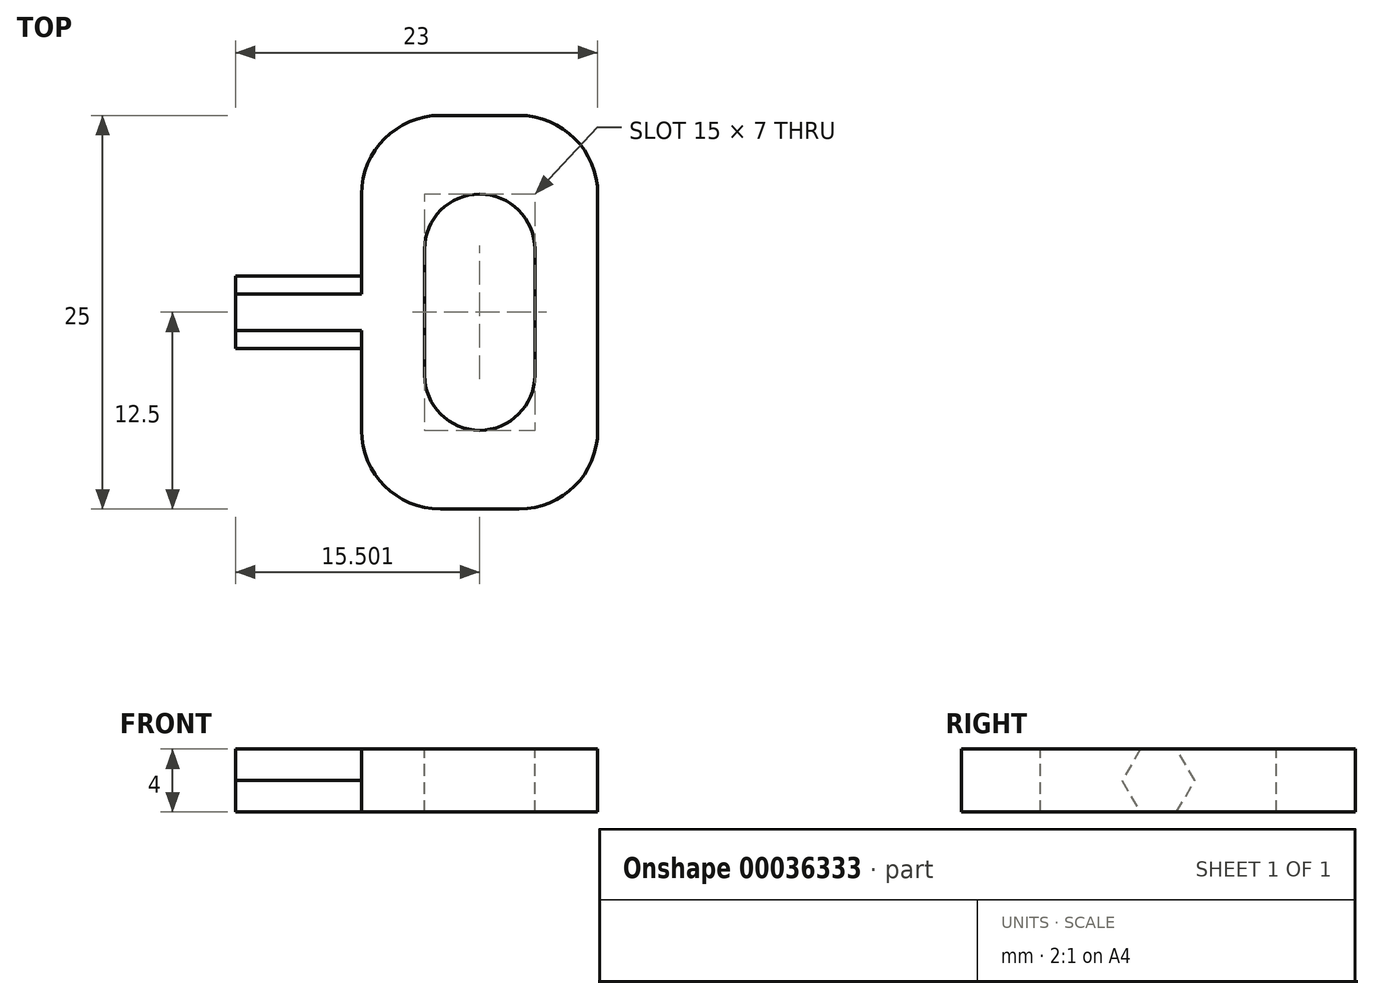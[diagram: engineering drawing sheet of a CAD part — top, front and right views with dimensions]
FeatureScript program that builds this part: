
annotation { "Feature Type Name" : "Feature", "Feature Type Description" : "" }
export const myFeature = defineFeature(function(context is Context, id is Id, definition is map)
    precondition{}
    {
        {
            var Q0;
            Q0=qCreatedBy(makeId("Top.planeOp"),FACE);
            var sketch = newSketch(context, id + "F0", { "sketchPlane" : qUnion([Q0])});
            skLineSegment(sketch, "E0.bottom", {"start": v(30.78, 0) * mm, "end": v(45.78, 0) * mm});
            skLineSegment(sketch, "E0.top", {"start": v(30.78, -25) * mm, "end": v(45.78, -25) * mm});
            skLineSegment(sketch, "E0.left", {"start": v(30.78, 0) * mm, "end": v(30.78, -25) * mm});
            skLineSegment(sketch, "E0.right", {"start": v(45.78, 0) * mm, "end": v(45.78, -25) * mm});
            skSolve(sketch);
        }
        {
            var Q0;
            Q0=makeQuery(id+"F0.imprint","IMPRINT",FACE,{"disambiguationData":[TD([[makeQuery(id+"F0.imprint","IMPRINT",EDGE,{"derivedFrom":sQuery(id+"F0.wireOp",EDGE,"E0.bottom")}),-1.0]])]});
            extrude(context, id + "F1", {"entities" : qUnion([Q0]), "depth" : 4 * mm});
        }
        {
            var Q0;
            Q0=makeQuery(id+"F1.opExtrude","SWEPT_FACE",FACE,{"disambiguationData":[OSD([sQuery(id+"F0.wireOp",EDGE,"E0.left")])]});
            var sketch = newSketch(context, id + "F2", { "sketchPlane" : qUnion([Q0])});
            skCircle(sketch, "E1.cCircle", {"center": v(12.5, 2) * mm, "radius": 2 * mm, "construction": true});
            skPoint(sketch, "E1.cCircle.centerSnap0", {"position": v(12.5, 4) * mm});
            skPoint(sketch, "E1.cCircle.centerSnap1", {"position": v(25, 2) * mm});
            skLineSegment(sketch, "E1.0", {"start": v(14.8, 2) * mm, "end": v(13.65, 0) * mm});
            skLineSegment(sketch, "E1.1", {"start": v(13.65, 0) * mm, "end": v(11.35, 0) * mm});
            skLineSegment(sketch, "E1.2", {"start": v(11.35, 0) * mm, "end": v(10.2, 2) * mm});
            skLineSegment(sketch, "E1.3", {"start": v(10.2, 2) * mm, "end": v(11.35, 4) * mm});
            skLineSegment(sketch, "E1.4", {"start": v(11.35, 4) * mm, "end": v(13.65, 4) * mm});
            skLineSegment(sketch, "E1.5", {"start": v(13.65, 4) * mm, "end": v(14.8, 2) * mm});
            skPoint(sketch, "E1.0.midPoint", {"position": v(14.23, 1) * mm});
            skSolve(sketch);
        }
        {
            var Q0;
            Q0=makeQuery(id+"F2.imprint","IMPRINT",FACE,{"disambiguationData":[TD([[makeQuery(id+"F2.imprint","IMPRINT",EDGE,{"derivedFrom":sQuery(id+"F2.wireOp",EDGE,"E1.0")}),-1.0]])]});
            extrude(context, id + "F3", {"entities" : qUnion([Q0]), "operationType" : NewBodyOperationType.ADD, "depth" : 8 * mm});
        }
        {
            var Q0;
            Q0=makeQuery(id+"F3.boolean.opBoolean","MERGE",FACE,{"derivedFrom":[makeQuery(id+"F1.opExtrude","CAP_FACE",FACE,{"disambiguationData":[OSD([sQuery(id+"F0.wireOp",EDGE,"E0.bottom"),sQuery(id+"F0.wireOp",EDGE,"E0.top"),sQuery(id+"F0.wireOp",EDGE,"E0.left"),sQuery(id+"F0.wireOp",EDGE,"E0.right")])],"isStart":false}),makeQuery(id+"F3.opExtrude","SWEPT_FACE",FACE,{"disambiguationData":[OSD([sQuery(id+"F2.wireOp",EDGE,"E1.4")])]})]});
            var sketch = newSketch(context, id + "F4", { "sketchPlane" : qUnion([Q0])});
            skCircle(sketch, "E2", {"center": v(38.28, -16.5) * mm, "radius": 3.5 * mm});
            skCircle(sketch, "E3", {"center": v(38.28, -8.5) * mm, "radius": 3.5 * mm});
            skPoint(sketch, "E4.endSnap0", {"position": v(45.78, -12.5) * mm});
            skLineSegment(sketch, "E5.bottom", {"start": v(41.78, -16.5) * mm, "end": v(34.78, -16.5) * mm});
            skLineSegment(sketch, "E5.top", {"start": v(41.78, -8.5) * mm, "end": v(34.78, -8.5) * mm});
            skLineSegment(sketch, "E5.left", {"start": v(41.78, -16.5) * mm, "end": v(41.78, -8.5) * mm});
            skLineSegment(sketch, "E5.right", {"start": v(34.78, -16.5) * mm, "end": v(34.78, -8.5) * mm});
            skLineSegment(sketch, "E6", {"start": v(38.28, 0) * mm, "end": v(38.28, -8.5) * mm, "construction": true});
            skLineSegment(sketch, "E7", {"start": v(38.28, -25) * mm, "end": v(38.28, -16.5) * mm, "construction": true});
            skLineSegment(sketch, "E8", {"start": v(38.28, -8.5) * mm, "end": v(38.28, -16.5) * mm, "construction": true});
            skSolve(sketch);
        }
        {
            var Q0;
            {var subQ0=sQuery(id+"F4.wireOp",EDGE,"E5.top");var subQ1=sQuery(id+"F4.wireOp",EDGE,"E2");var subQ5=makeQuery(id+"F4.imprint","INTERSECT",VERTEX,{"disambiguationData":[OD(0.0)],"derivedFrom":[subQ1,subQ0]});Q0=makeQuery(id+"F4.imprint","IMPRINT",FACE,{"disambiguationData":[TD([[makeQuery(id+"F4.imprint","IMPRINT",EDGE,{"disambiguationData":[TD([[subQ5,-1.0]])],"derivedFrom":subQ1}),-1.0]])]});}
            var Q1;
            {var subQ0=sQuery(id+"F4.wireOp",EDGE,"E5.top");var subQ1=sQuery(id+"F4.wireOp",EDGE,"E2");var subQ3=makeQuery(id+"F4.imprint","INTERSECT",VERTEX,{"disambiguationData":[OD(0.0)],"derivedFrom":[subQ1,subQ0]});Q1=makeQuery(id+"F4.imprint","IMPRINT",FACE,{"disambiguationData":[TD([[makeQuery(id+"F4.imprint","IMPRINT",EDGE,{"disambiguationData":[TD([[subQ3,-1.0]])],"derivedFrom":subQ1}),1.0]])]});}
            var Q2;
            {var subQ1=sQuery(id+"F4.wireOp",EDGE,"E2");var subQ5=sQuery(id+"F4.wireOp",EDGE,"E3");var subQ8=makeQuery(id+"F4.imprint","INTERSECT",VERTEX,{"disambiguationData":[OD(0.0)],"derivedFrom":[subQ1,subQ5]});Q2=makeQuery(id+"F4.imprint","IMPRINT",FACE,{"disambiguationData":[TD([[makeQuery(id+"F4.imprint","IMPRINT",EDGE,{"disambiguationData":[TD([[subQ8,-1.0]])],"derivedFrom":subQ1}),1.0]])]});}
            var Q3;
            {var subQ0=sQuery(id+"F4.wireOp",EDGE,"E5.top");var subQ1=sQuery(id+"F4.wireOp",EDGE,"E2");var subQ2=makeQuery(id+"F4.imprint","INTERSECT",VERTEX,{"disambiguationData":[OD(1.0)],"derivedFrom":[subQ1,subQ0]});Q3=makeQuery(id+"F4.imprint","IMPRINT",FACE,{"disambiguationData":[TD([[makeQuery(id+"F4.imprint","IMPRINT",EDGE,{"disambiguationData":[TD([[subQ2,-1.0]])],"derivedFrom":subQ1}),-1.0]])]});}
            var Q4;
            {var subQ1=sQuery(id+"F4.wireOp",EDGE,"E2");var subQ3=sQuery(id+"F4.wireOp",EDGE,"E3");var subQ5=makeQuery(id+"F4.imprint","INTERSECT",VERTEX,{"disambiguationData":[OD(0.0)],"derivedFrom":[subQ1,subQ3]});Q4=makeQuery(id+"F4.imprint","IMPRINT",FACE,{"disambiguationData":[TD([[makeQuery(id+"F4.imprint","IMPRINT",EDGE,{"disambiguationData":[TD([[subQ5,-1.0]])],"derivedFrom":subQ1}),-1.0]])]});}
            var Q5;
            {var subQ1=sQuery(id+"F4.wireOp",EDGE,"E3");var subQ3=sQuery(id+"F4.wireOp",EDGE,"E2");var subQ5=makeQuery(id+"F4.imprint","INTERSECT",VERTEX,{"disambiguationData":[OD(0.0)],"derivedFrom":[subQ3,subQ1]});Q5=makeQuery(id+"F4.imprint","IMPRINT",FACE,{"disambiguationData":[TD([[makeQuery(id+"F4.imprint","IMPRINT",EDGE,{"disambiguationData":[TD([[subQ5,1.0]])],"derivedFrom":subQ1}),-1.0]])]});}
            var Q6;
            {var subQ0=sQuery(id+"F4.wireOp",EDGE,"E5.bottom");var subQ1=sQuery(id+"F4.wireOp",EDGE,"E3");var subQ2=makeQuery(id+"F4.imprint","INTERSECT",VERTEX,{"disambiguationData":[OD(0.0)],"derivedFrom":[subQ1,subQ0]});Q6=makeQuery(id+"F4.imprint","IMPRINT",FACE,{"disambiguationData":[TD([[makeQuery(id+"F4.imprint","IMPRINT",EDGE,{"disambiguationData":[TD([[subQ2,-1.0]])],"derivedFrom":subQ1}),-1.0]])]});}
            var Q7;
            {var subQ0=sQuery(id+"F4.wireOp",EDGE,"E5.bottom");var subQ1=sQuery(id+"F4.wireOp",EDGE,"E3");var subQ3=makeQuery(id+"F4.imprint","INTERSECT",VERTEX,{"disambiguationData":[OD(0.0)],"derivedFrom":[subQ1,subQ0]});Q7=makeQuery(id+"F4.imprint","IMPRINT",FACE,{"disambiguationData":[TD([[makeQuery(id+"F4.imprint","IMPRINT",EDGE,{"disambiguationData":[TD([[subQ3,-1.0]])],"derivedFrom":subQ1}),1.0]])]});}
            var Q8;
            {var subQ1=sQuery(id+"F4.wireOp",EDGE,"E3");var subQ3=sQuery(id+"F4.wireOp",EDGE,"E2");var subQ5=makeQuery(id+"F4.imprint","INTERSECT",VERTEX,{"disambiguationData":[OD(1.0)],"derivedFrom":[subQ3,subQ1]});Q8=makeQuery(id+"F4.imprint","IMPRINT",FACE,{"disambiguationData":[TD([[makeQuery(id+"F4.imprint","IMPRINT",EDGE,{"disambiguationData":[TD([[subQ5,-1.0]])],"derivedFrom":subQ1}),-1.0]])]});}
            var Q9;
            {var subQ0=sQuery(id+"F4.wireOp",EDGE,"E5.right");Q9=makeQuery(id+"F4.imprint","IMPRINT",FACE,{"disambiguationData":[TD([[makeQuery(id+"F4.imprint","IMPRINT",EDGE,{"derivedFrom":subQ0}),-1.0]])]});}
            var Q10;
            {var subQ0=sQuery(id+"F4.wireOp",EDGE,"E5.left");Q10=makeQuery(id+"F4.imprint","IMPRINT",FACE,{"disambiguationData":[TD([[makeQuery(id+"F4.imprint","IMPRINT",EDGE,{"derivedFrom":subQ0}),1.0]])]});}
            extrude(context, id + "F5", {"entities" : qUnion([Q0, Q1, Q2, Q3, Q4, Q5, Q6, Q7, Q8, Q9, Q10]), "operationType" : NewBodyOperationType.REMOVE, "endBound" : BoundingType.UP_TO_NEXT, "oppositeDirection" : true, "depth" : 25 * mm});
        }
        {
            var Q0;
            Q0=makeQuery(id+"F1.opExtrude","SWEPT_EDGE",EDGE,{"disambiguationData":[OSD([sQuery(id+"F0.wireOp",EDGE,"E0.bottom"),sQuery(id+"F0.wireOp",EDGE,"E0.right")])]});
            var Q1;
            Q1=makeQuery(id+"F1.opExtrude","SWEPT_EDGE",EDGE,{"disambiguationData":[OSD([sQuery(id+"F0.wireOp",EDGE,"E0.bottom"),sQuery(id+"F0.wireOp",EDGE,"E0.left")])]});
            var Q2;
            Q2=makeQuery(id+"F1.opExtrude","SWEPT_EDGE",EDGE,{"disambiguationData":[OSD([sQuery(id+"F0.wireOp",EDGE,"E0.top"),sQuery(id+"F0.wireOp",EDGE,"E0.right")])]});
            var Q3;
            Q3=makeQuery(id+"F1.opExtrude","SWEPT_EDGE",EDGE,{"disambiguationData":[OSD([sQuery(id+"F0.wireOp",EDGE,"E0.top"),sQuery(id+"F0.wireOp",EDGE,"E0.left")])]});
            fillet(context, id + "F6", {"entities" : qUnion([Q0, Q1, Q2, Q3]), "radius" : 5 * mm, "tangentPropagation" : true, "allowEdgeOverflow" : false});
        }
    });
